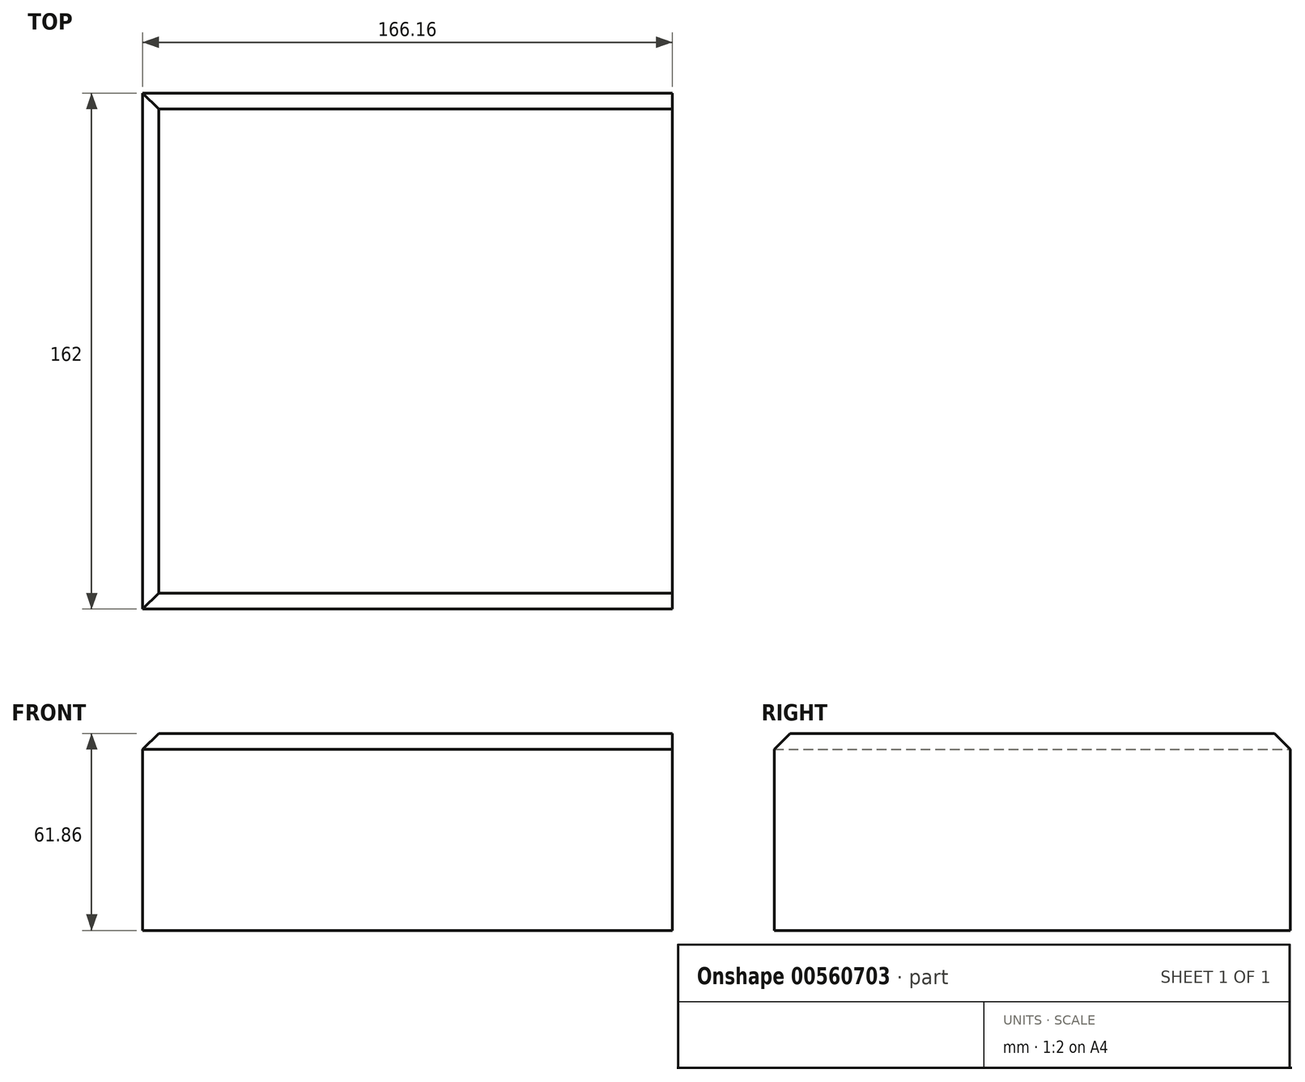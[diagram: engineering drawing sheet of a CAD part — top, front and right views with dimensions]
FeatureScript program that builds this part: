
annotation { "Feature Type Name" : "Feature", "Feature Type Description" : "" }
export const myFeature = defineFeature(function(context is Context, id is Id, definition is map)
    precondition{}
    {
        {
            var Q0;
            Q0=qCreatedBy(makeId("Front.planeOp"),FACE);
            var sketch = newSketch(context, id + "F0", { "sketchPlane" : qUnion([Q0])});
            skLineSegment(sketch, "E0.bottom", {"start": v(-83.08, 30.93) * mm, "end": v(83.08, 30.93) * mm});
            skLineSegment(sketch, "E0.top", {"start": v(-83.08, -30.93) * mm, "end": v(83.08, -30.93) * mm});
            skLineSegment(sketch, "E0.left", {"start": v(-83.08, 30.93) * mm, "end": v(-83.08, -30.93) * mm});
            skLineSegment(sketch, "E0.right", {"start": v(83.08, 30.93) * mm, "end": v(83.08, -30.93) * mm});
            skPoint(sketch, "E0.middle", {"position": v(0, 0) * mm});
            skSolve(sketch);
        }
        {
            var Q0;
            Q0 = qSketchRegion(id + "F0", true);
            extrude(context, id + "F1", {"entities" : qUnion([Q0]), "depth" : 81 * mm, "offsetDistance" : 25 * mm});
        }
        {
            var Q0;
            Q0=makeQuery(id+"F1.opExtrude","CAP_EDGE",EDGE,{"disambiguationData":[OSD([sQuery(id+"F0.wireOp",EDGE,"E0.bottom")])],"isStart":false});
            var Q1;
            Q1=makeQuery(id+"F1.opExtrude","SWEPT_EDGE",EDGE,{"disambiguationData":[OSD([sQuery(id+"F0.wireOp",EDGE,"E0.bottom"),sQuery(id+"F0.wireOp",EDGE,"E0.left")])]});
            chamfer(context, id + "F2", {"entities" : qUnion([Q0, Q1]), "width" : 5 * mm, "tangentPropagation" : true});
        }
        {
            var Q0;
            Q0=makeQuery(id+"F1.opExtrude","SWEPT_BODY",BODY,{"disambiguationData":[OSD([sQuery(id+"F0.wireOp",EDGE,"E0.bottom"),sQuery(id+"F0.wireOp",EDGE,"E0.top"),sQuery(id+"F0.wireOp",EDGE,"E0.left"),sQuery(id+"F0.wireOp",EDGE,"E0.right")])]});
            var Q1;
            Q1=makeQuery(id+"F1.opExtrude","CAP_FACE",FACE,{"disambiguationData":[OSD([sQuery(id+"F0.wireOp",EDGE,"E0.bottom"),sQuery(id+"F0.wireOp",EDGE,"E0.top"),sQuery(id+"F0.wireOp",EDGE,"E0.left"),sQuery(id+"F0.wireOp",EDGE,"E0.right")])],"isStart":true});
            mirror(context, id + "F3", {"operationType" : NewBodyOperationType.ADD, "entities" : qUnion([Q0]), "mirrorPlane" : qUnion([Q1])});
        }
    });
